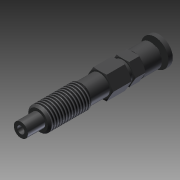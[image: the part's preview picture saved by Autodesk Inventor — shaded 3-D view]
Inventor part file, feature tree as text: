
AUTODESK INVENTOR PART (.ipt)
format: ipt  version: 2011 SP1 (Build 150282100, 282)  size: 177,152 bytes
history: native  units: mm
features: other x28, sketch x3, extrude x2, revolve x1, thread x1
ambient origin geometry x8: Origin, YZ Plane, XZ Plane, XY Plane, X Axis, Y Axis, Z Axis, Center Point
bodies: Solid1 (feature_tree)
feature tree (35):
  revolve  "Revolution1"  [1 undecoded]
  thread  "Thread1"  [1 undecoded]
  extrude  "Extrusion1"  [1 undecoded]
  extrude  "Extrusion2"  [1 undecoded]
  other  "BUFFER_DUMMY_XY"
  other  "BUFFER_DUMMY_YZ"
  other  "BUFFER_DUMMY_ZX"
  other  "BUFFER_DUMMY_X"
  other  "BUFFER_DUMMY_Y"
  other  "BUFFER_DUMMY_Z"
  other  "BUFFER_DUMMY_Center"
  other  "BUFFER_NUT1_XY"
  other  "BUFFER_NUT1_YZ"
  other  "BUFFER_NUT1_ZX"
  other  "BUFFER_NUT1_X"
  other  "BUFFER_NUT1_Y"
  other  "BUFFER_NUT1_Z"
  other  "BUFFER_NUT1_Center"
  other  "BUFFER_NUT2_XY"
  other  "BUFFER_NUT2_YZ"
  other  "BUFFER_NUT2_ZX"
  other  "BUFFER_NUT2_X"
  other  "BUFFER_NUT2_Y"
  other  "BUFFER_NUT2_Z"
  other  "BUFFER_NUT2_Center"
  other  "BUFFER_PLATE_XY"
  other  "BUFFER_PLATE_YZ"
  other  "BUFFER_PLATE_ZX"
  other  "BUFFER_PLATE_X"
  other  "BUFFER_PLATE_Y"
  other  "BUFFER_PLATE_Z"
  other  "BUFFER_PLATE_Center"
  sketch  "Sketch_9"  dims[d0=360.0deg d1=13.773mm d2=0.0mm d3=3.8mm d4=0.0mm]
  sketch  "Sketch_10"  dims[d5=6.65mm d6=0.0mm]
  sketch  "Sketch_11"
note: 4 required parameter values undecoded (feature->parameter linkage not recoverable at this tier; creation-order binding heuristic only, values carry confidence <= 0.55)